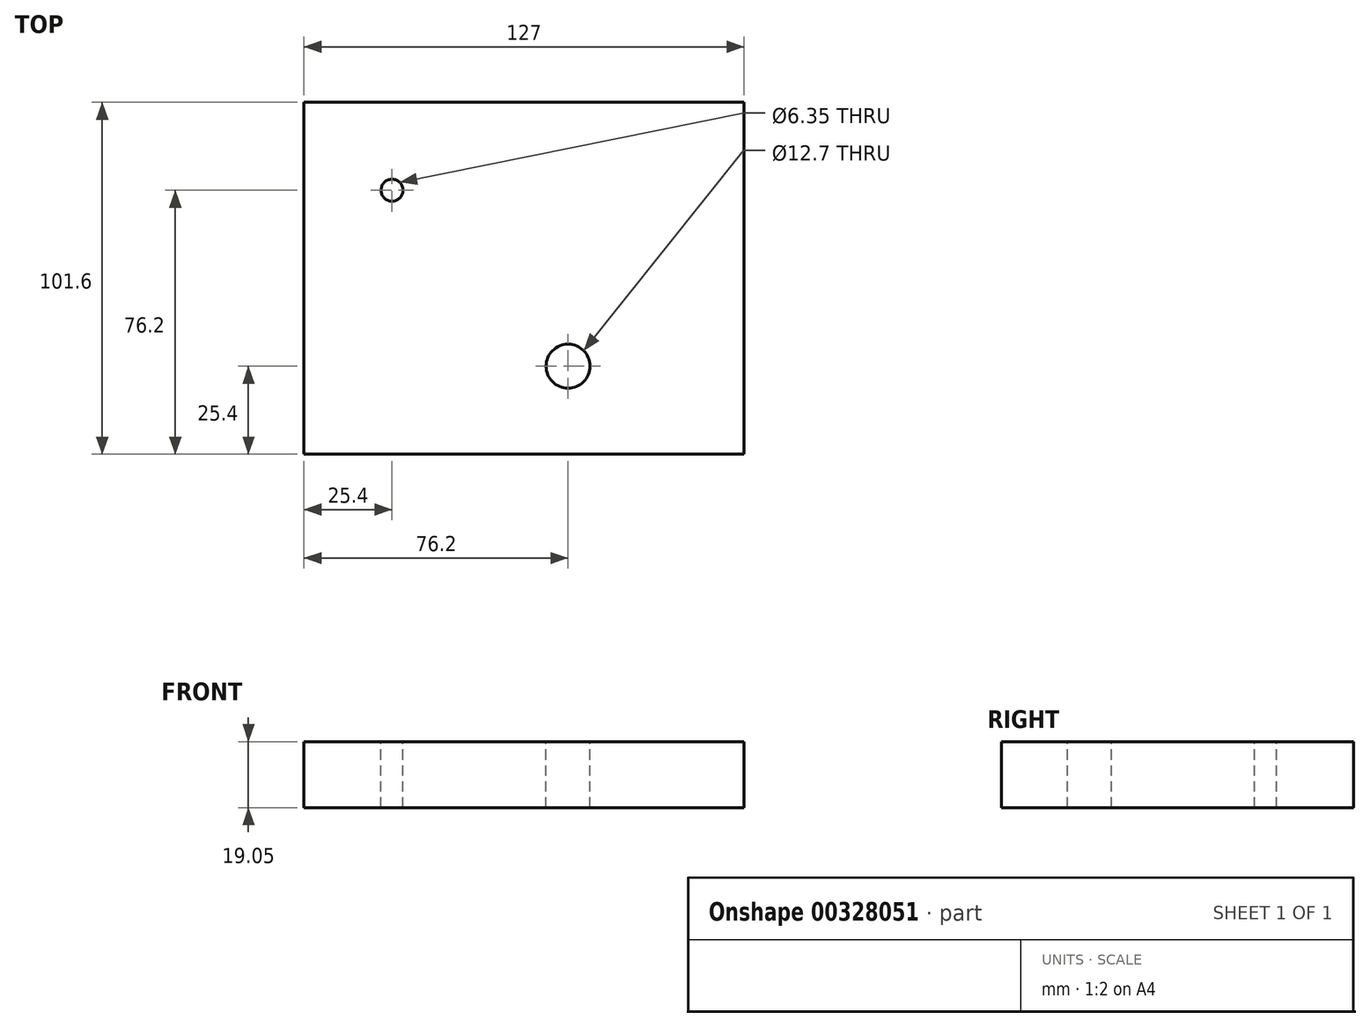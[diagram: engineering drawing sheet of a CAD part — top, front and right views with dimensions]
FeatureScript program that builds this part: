
annotation { "Feature Type Name" : "Feature", "Feature Type Description" : "" }
export const myFeature = defineFeature(function(context is Context, id is Id, definition is map)
    precondition{}
    {
        {
            var Q0;
            Q0=qCreatedBy(makeId("Top.planeOp"),FACE);
            var sketch = newSketch(context, id + "F0", { "sketchPlane" : qUnion([Q0])});
            skLineSegment(sketch, "E0.bottom", {"start": v(-63.5, 50.8) * mm, "end": v(63.5, 50.8) * mm});
            skLineSegment(sketch, "E0.top", {"start": v(-63.5, -50.8) * mm, "end": v(63.5, -50.8) * mm});
            skLineSegment(sketch, "E0.left", {"start": v(-63.5, 50.8) * mm, "end": v(-63.5, -50.8) * mm});
            skLineSegment(sketch, "E0.right", {"start": v(63.5, 50.8) * mm, "end": v(63.5, -50.8) * mm});
            skPoint(sketch, "E0.middle", {"position": v(0, 0) * mm});
            skSolve(sketch);
        }
        {
            var Q0;
            Q0=makeQuery(id+"F0.imprint","IMPRINT",FACE,{"disambiguationData":[TD([[makeQuery(id+"F0.imprint","IMPRINT",EDGE,{"derivedFrom":sQuery(id+"F0.wireOp",EDGE,"E0.bottom")}),-1.0]])]});
            extrude(context, id + "F1", {"entities" : qUnion([Q0]), "depth" : 19.05 * mm});
        }
        {
            var Q0;
            Q0=makeQuery(id+"F1.opExtrude","CAP_FACE",FACE,{"disambiguationData":[OSD([sQuery(id+"F0.wireOp",EDGE,"E0.bottom"),sQuery(id+"F0.wireOp",EDGE,"E0.top"),sQuery(id+"F0.wireOp",EDGE,"E0.left"),sQuery(id+"F0.wireOp",EDGE,"E0.right")])],"isStart":false});
            var sketch = newSketch(context, id + "F2", { "sketchPlane" : qUnion([Q0])});
            skCircle(sketch, "E1", {"center": v(-38.1, 25.4) * mm, "radius": 3.18 * mm});
            skSolve(sketch);
        }
        {
            var Q0;
            Q0=makeQuery(id+"F2.imprint","IMPRINT",FACE,{"disambiguationData":[TD([[makeQuery(id+"F2.imprint","IMPRINT",EDGE,{"derivedFrom":sQuery(id+"F2.wireOp",EDGE,"E1")}),1.0]])]});
            extrude(context, id + "F3", {"entities" : qUnion([Q0]), "operationType" : NewBodyOperationType.REMOVE, "oppositeDirection" : true, "depth" : 25.4 * mm});
        }
        {
            var Q0;
            Q0=makeQuery(id+"F1.opExtrude","CAP_FACE",FACE,{"disambiguationData":[OSD([sQuery(id+"F0.wireOp",EDGE,"E0.bottom"),sQuery(id+"F0.wireOp",EDGE,"E0.top"),sQuery(id+"F0.wireOp",EDGE,"E0.left"),sQuery(id+"F0.wireOp",EDGE,"E0.right")])],"isStart":false});
            var sketch = newSketch(context, id + "F4", { "sketchPlane" : qUnion([Q0])});
            skCircle(sketch, "E2", {"center": v(12.7, -25.4) * mm, "radius": 6.35 * mm});
            skSolve(sketch);
        }
        {
            var Q0;
            Q0=makeQuery(id+"F4.imprint","IMPRINT",FACE,{"disambiguationData":[TD([[makeQuery(id+"F4.imprint","IMPRINT",EDGE,{"derivedFrom":sQuery(id+"F4.wireOp",EDGE,"E2")}),1.0]])]});
            extrude(context, id + "F5", {"entities" : qUnion([Q0]), "operationType" : NewBodyOperationType.REMOVE, "oppositeDirection" : true, "depth" : 25.4 * mm});
        }
    });
